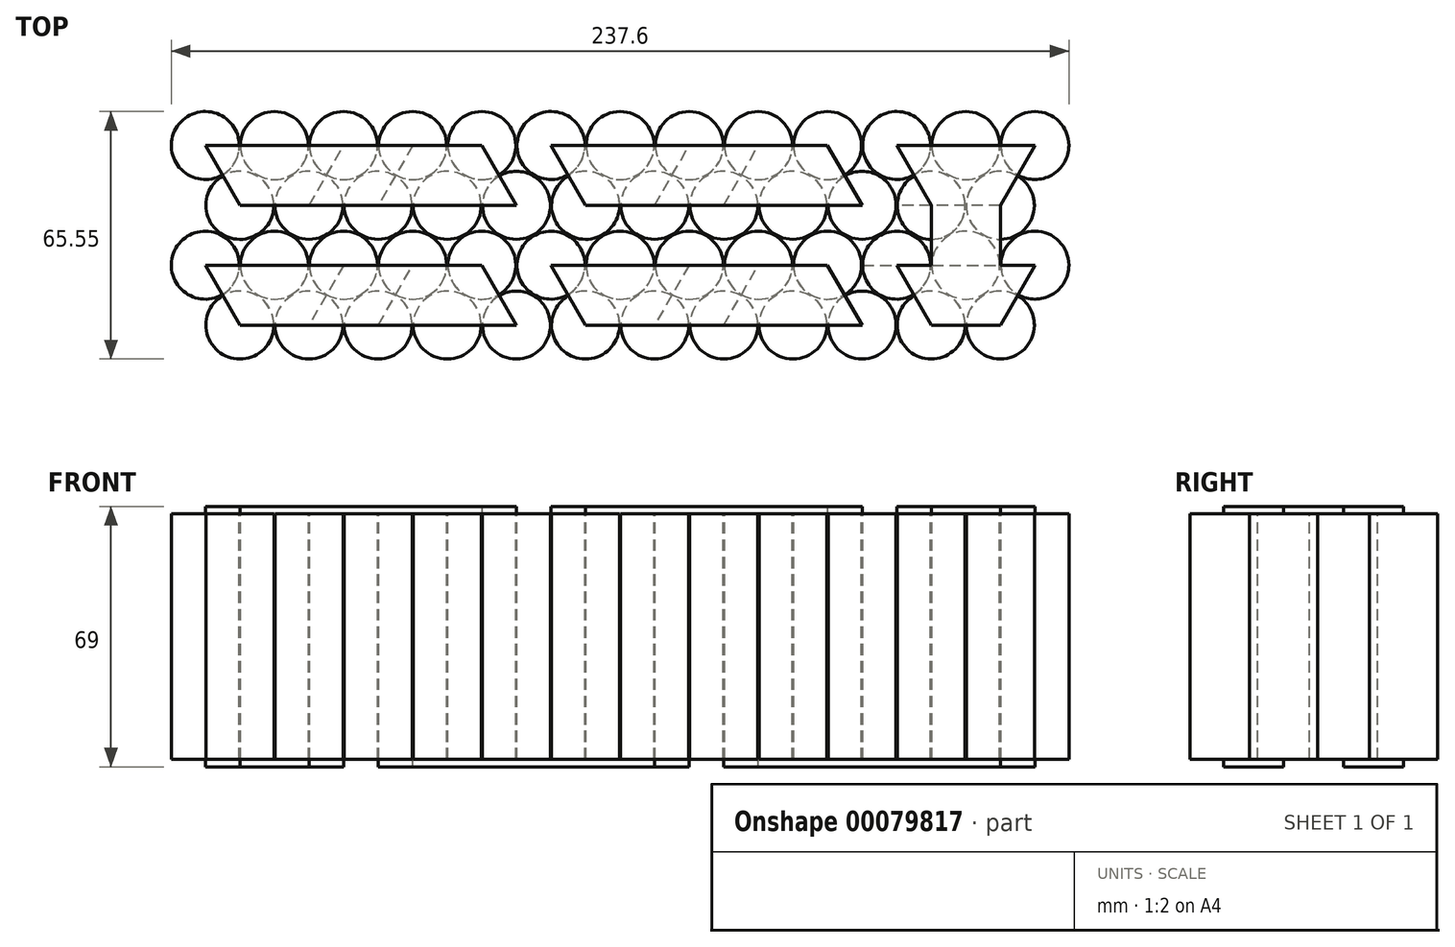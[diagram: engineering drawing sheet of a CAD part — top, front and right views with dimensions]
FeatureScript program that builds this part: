
annotation { "Feature Type Name" : "Feature", "Feature Type Description" : "" }
export const myFeature = defineFeature(function(context is Context, id is Id, definition is map)
    precondition{}
    {
        {
            var Q0;
            Q0=qCreatedBy(makeId("Top.planeOp"),FACE);
            var sketch = newSketch(context, id + "F0", { "sketchPlane" : qUnion([Q0])});
            skLineSegment(sketch, "E0", {"start": v(0, 0) * mm, "end": v(9.15, 15.85) * mm, "construction": true});
            skLineSegment(sketch, "E1", {"start": v(9.15, 15.85) * mm, "end": v(18.3, 0) * mm, "construction": true});
            skLineSegment(sketch, "E2", {"start": v(18.3, 0) * mm, "end": v(9.15, -15.85) * mm, "construction": true});
            skLineSegment(sketch, "E3", {"start": v(9.15, -15.85) * mm, "end": v(0, 0) * mm, "construction": true});
            skLineSegment(sketch, "E4", {"start": v(9.15, 15.85) * mm, "end": v(0, 31.7) * mm, "construction": true});
            skLineSegment(sketch, "E5", {"start": v(0, 31.7) * mm, "end": v(18.3, 31.7) * mm, "construction": true});
            skLineSegment(sketch, "E6", {"start": v(18.3, 31.7) * mm, "end": v(9.15, 15.85) * mm, "construction": true});
            skLineSegment(sketch, "E7", {"start": v(18.3, 31.7) * mm, "end": v(27.45, 15.85) * mm, "construction": true});
            skLineSegment(sketch, "E8", {"start": v(27.45, 15.85) * mm, "end": v(18.3, 0) * mm, "construction": true});
            skLineSegment(sketch, "E9", {"start": v(18.3, 0) * mm, "end": v(27.45, -15.85) * mm, "construction": true});
            skLineSegment(sketch, "E10", {"start": v(27.45, -15.85) * mm, "end": v(9.15, -15.85) * mm, "construction": true});
            skCircle(sketch, "E11", {"center": v(0, 31.7) * mm, "radius": 9 * mm});
            skCircle(sketch, "E12", {"center": v(18.3, 31.7) * mm, "radius": 9 * mm});
            skCircle(sketch, "E13", {"center": v(27.45, 15.85) * mm, "radius": 9 * mm});
            skCircle(sketch, "E14", {"center": v(9.15, 15.85) * mm, "radius": 9 * mm});
            skCircle(sketch, "E15", {"center": v(0, 0) * mm, "radius": 9 * mm});
            skCircle(sketch, "E16", {"center": v(18.3, 0) * mm, "radius": 9 * mm});
            skCircle(sketch, "E17", {"center": v(9.15, -15.85) * mm, "radius": 9 * mm});
            skCircle(sketch, "E18", {"center": v(27.45, -15.85) * mm, "radius": 9 * mm});
            skLineSegment(sketch, "E19", {"start": v(0, 40.7) * mm, "end": v(18.3, 40.7) * mm, "construction": true});
            skLineSegment(sketch, "E20", {"start": v(9.15, -24.85) * mm, "end": v(27.45, -24.85) * mm, "construction": true});
            skCircle(sketch, "E21.1.0.0", {"center": v(54.9, 0) * mm, "radius": 9 * mm});
            skCircle(sketch, "E21.1.0.1", {"center": v(64.05, -15.85) * mm, "radius": 9 * mm});
            skLineSegment(sketch, "E21.1.0.2", {"start": v(45.75, -24.85) * mm, "end": v(64.05, -24.85) * mm, "construction": true});
            skCircle(sketch, "E21.1.0.3", {"center": v(54.9, 31.7) * mm, "radius": 9 * mm});
            skLineSegment(sketch, "E21.1.0.4", {"start": v(54.9, 31.7) * mm, "end": v(64.05, 15.85) * mm, "construction": true});
            skLineSegment(sketch, "E21.1.0.5", {"start": v(64.05, 15.85) * mm, "end": v(54.9, 0) * mm, "construction": true});
            skLineSegment(sketch, "E21.1.0.6", {"start": v(54.9, 31.7) * mm, "end": v(45.75, 15.85) * mm, "construction": true});
            skLineSegment(sketch, "E21.1.0.7", {"start": v(54.9, 0) * mm, "end": v(64.05, -15.85) * mm, "construction": true});
            skLineSegment(sketch, "E21.1.0.8", {"start": v(36.6, 31.7) * mm, "end": v(54.9, 31.7) * mm, "construction": true});
            skLineSegment(sketch, "E21.1.0.9", {"start": v(64.05, -15.85) * mm, "end": v(45.75, -15.85) * mm, "construction": true});
            skLineSegment(sketch, "E21.1.0.10", {"start": v(45.75, 15.85) * mm, "end": v(36.6, 31.7) * mm, "construction": true});
            skLineSegment(sketch, "E21.1.0.11", {"start": v(45.75, -15.85) * mm, "end": v(36.6, 0) * mm, "construction": true});
            skCircle(sketch, "E21.1.0.12", {"center": v(36.6, 31.7) * mm, "radius": 9 * mm});
            skCircle(sketch, "E21.1.0.13", {"center": v(45.75, 15.85) * mm, "radius": 9 * mm});
            skCircle(sketch, "E21.1.0.14", {"center": v(36.6, 0) * mm, "radius": 9 * mm});
            skCircle(sketch, "E21.1.0.15", {"center": v(45.75, -15.85) * mm, "radius": 9 * mm});
            skLineSegment(sketch, "E21.1.0.16", {"start": v(54.9, 0) * mm, "end": v(45.75, -15.85) * mm, "construction": true});
            skLineSegment(sketch, "E21.1.0.17", {"start": v(45.75, 15.85) * mm, "end": v(54.9, 0) * mm, "construction": true});
            skLineSegment(sketch, "E21.1.0.18", {"start": v(36.6, 0) * mm, "end": v(45.75, 15.85) * mm, "construction": true});
            skCircle(sketch, "E21.1.0.19", {"center": v(64.05, 15.85) * mm, "radius": 9 * mm});
            skLineSegment(sketch, "E21.1.0.20", {"start": v(36.6, 40.7) * mm, "end": v(54.9, 40.7) * mm, "construction": true});
            skCircle(sketch, "E21.2.0.0", {"center": v(91.5, 0) * mm, "radius": 9 * mm});
            skCircle(sketch, "E21.2.0.1", {"center": v(100.65, -15.85) * mm, "radius": 9 * mm});
            skLineSegment(sketch, "E21.2.0.2", {"start": v(82.35, -24.85) * mm, "end": v(100.65, -24.85) * mm, "construction": true});
            skCircle(sketch, "E21.2.0.3", {"center": v(91.5, 31.7) * mm, "radius": 9 * mm});
            skLineSegment(sketch, "E21.2.0.4", {"start": v(91.5, 31.7) * mm, "end": v(100.65, 15.85) * mm, "construction": true});
            skLineSegment(sketch, "E21.2.0.5", {"start": v(100.65, 15.85) * mm, "end": v(91.5, 0) * mm, "construction": true});
            skLineSegment(sketch, "E21.2.0.6", {"start": v(91.5, 31.7) * mm, "end": v(82.35, 15.85) * mm, "construction": true});
            skLineSegment(sketch, "E21.2.0.7", {"start": v(91.5, 0) * mm, "end": v(100.65, -15.85) * mm, "construction": true});
            skLineSegment(sketch, "E21.2.0.8", {"start": v(73.2, 31.7) * mm, "end": v(91.5, 31.7) * mm, "construction": true});
            skLineSegment(sketch, "E21.2.0.9", {"start": v(100.65, -15.85) * mm, "end": v(82.35, -15.85) * mm, "construction": true});
            skLineSegment(sketch, "E21.2.0.10", {"start": v(82.35, 15.85) * mm, "end": v(73.2, 31.7) * mm, "construction": true});
            skLineSegment(sketch, "E21.2.0.11", {"start": v(82.35, -15.85) * mm, "end": v(73.2, 0) * mm, "construction": true});
            skCircle(sketch, "E21.2.0.12", {"center": v(73.2, 31.7) * mm, "radius": 9 * mm});
            skCircle(sketch, "E21.2.0.13", {"center": v(82.35, 15.85) * mm, "radius": 9 * mm});
            skCircle(sketch, "E21.2.0.14", {"center": v(73.2, 0) * mm, "radius": 9 * mm});
            skCircle(sketch, "E21.2.0.15", {"center": v(82.35, -15.85) * mm, "radius": 9 * mm});
            skLineSegment(sketch, "E21.2.0.16", {"start": v(91.5, 0) * mm, "end": v(82.35, -15.85) * mm, "construction": true});
            skLineSegment(sketch, "E21.2.0.17", {"start": v(82.35, 15.85) * mm, "end": v(91.5, 0) * mm, "construction": true});
            skLineSegment(sketch, "E21.2.0.18", {"start": v(73.2, 0) * mm, "end": v(82.35, 15.85) * mm, "construction": true});
            skCircle(sketch, "E21.2.0.19", {"center": v(100.65, 15.85) * mm, "radius": 9 * mm});
            skLineSegment(sketch, "E21.2.0.20", {"start": v(73.2, 40.7) * mm, "end": v(91.5, 40.7) * mm, "construction": true});
            skCircle(sketch, "E21.3.0.0", {"center": v(128.1, 0) * mm, "radius": 9 * mm});
            skCircle(sketch, "E21.3.0.1", {"center": v(137.25, -15.85) * mm, "radius": 9 * mm});
            skLineSegment(sketch, "E21.3.0.2", {"start": v(118.95, -24.85) * mm, "end": v(137.25, -24.85) * mm, "construction": true});
            skCircle(sketch, "E21.3.0.3", {"center": v(128.1, 31.7) * mm, "radius": 9 * mm});
            skLineSegment(sketch, "E21.3.0.4", {"start": v(128.1, 31.7) * mm, "end": v(137.25, 15.85) * mm, "construction": true});
            skLineSegment(sketch, "E21.3.0.5", {"start": v(137.25, 15.85) * mm, "end": v(128.1, 0) * mm, "construction": true});
            skLineSegment(sketch, "E21.3.0.6", {"start": v(128.1, 31.7) * mm, "end": v(118.95, 15.85) * mm, "construction": true});
            skLineSegment(sketch, "E21.3.0.7", {"start": v(128.1, 0) * mm, "end": v(137.25, -15.85) * mm, "construction": true});
            skLineSegment(sketch, "E21.3.0.8", {"start": v(109.8, 31.7) * mm, "end": v(128.1, 31.7) * mm, "construction": true});
            skLineSegment(sketch, "E21.3.0.9", {"start": v(137.25, -15.85) * mm, "end": v(118.95, -15.85) * mm, "construction": true});
            skLineSegment(sketch, "E21.3.0.10", {"start": v(118.95, 15.85) * mm, "end": v(109.8, 31.7) * mm, "construction": true});
            skLineSegment(sketch, "E21.3.0.11", {"start": v(118.95, -15.85) * mm, "end": v(109.8, 0) * mm, "construction": true});
            skCircle(sketch, "E21.3.0.12", {"center": v(109.8, 31.7) * mm, "radius": 9 * mm});
            skCircle(sketch, "E21.3.0.13", {"center": v(118.95, 15.85) * mm, "radius": 9 * mm});
            skCircle(sketch, "E21.3.0.14", {"center": v(109.8, 0) * mm, "radius": 9 * mm});
            skCircle(sketch, "E21.3.0.15", {"center": v(118.95, -15.85) * mm, "radius": 9 * mm});
            skLineSegment(sketch, "E21.3.0.16", {"start": v(128.1, 0) * mm, "end": v(118.95, -15.85) * mm, "construction": true});
            skLineSegment(sketch, "E21.3.0.17", {"start": v(118.95, 15.85) * mm, "end": v(128.1, 0) * mm, "construction": true});
            skLineSegment(sketch, "E21.3.0.18", {"start": v(109.8, 0) * mm, "end": v(118.95, 15.85) * mm, "construction": true});
            skCircle(sketch, "E21.3.0.19", {"center": v(137.25, 15.85) * mm, "radius": 9 * mm});
            skLineSegment(sketch, "E21.3.0.20", {"start": v(109.8, 40.7) * mm, "end": v(128.1, 40.7) * mm, "construction": true});
            skCircle(sketch, "E21.4.0.0", {"center": v(164.7, 0) * mm, "radius": 9 * mm});
            skCircle(sketch, "E21.4.0.1", {"center": v(173.85, -15.85) * mm, "radius": 9 * mm});
            skLineSegment(sketch, "E21.4.0.2", {"start": v(155.55, -24.85) * mm, "end": v(173.85, -24.85) * mm, "construction": true});
            skCircle(sketch, "E21.4.0.3", {"center": v(164.7, 31.7) * mm, "radius": 9 * mm});
            skLineSegment(sketch, "E21.4.0.4", {"start": v(164.7, 31.7) * mm, "end": v(173.85, 15.85) * mm, "construction": true});
            skLineSegment(sketch, "E21.4.0.5", {"start": v(173.85, 15.85) * mm, "end": v(164.7, 0) * mm, "construction": true});
            skLineSegment(sketch, "E21.4.0.6", {"start": v(164.7, 31.7) * mm, "end": v(155.55, 15.85) * mm, "construction": true});
            skLineSegment(sketch, "E21.4.0.7", {"start": v(164.7, 0) * mm, "end": v(173.85, -15.85) * mm, "construction": true});
            skLineSegment(sketch, "E21.4.0.8", {"start": v(146.4, 31.7) * mm, "end": v(164.7, 31.7) * mm, "construction": true});
            skLineSegment(sketch, "E21.4.0.9", {"start": v(173.85, -15.85) * mm, "end": v(155.55, -15.85) * mm, "construction": true});
            skLineSegment(sketch, "E21.4.0.10", {"start": v(155.55, 15.85) * mm, "end": v(146.4, 31.7) * mm, "construction": true});
            skLineSegment(sketch, "E21.4.0.11", {"start": v(155.55, -15.85) * mm, "end": v(146.4, 0) * mm, "construction": true});
            skCircle(sketch, "E21.4.0.12", {"center": v(146.4, 31.7) * mm, "radius": 9 * mm});
            skCircle(sketch, "E21.4.0.13", {"center": v(155.55, 15.85) * mm, "radius": 9 * mm});
            skCircle(sketch, "E21.4.0.14", {"center": v(146.4, 0) * mm, "radius": 9 * mm});
            skCircle(sketch, "E21.4.0.15", {"center": v(155.55, -15.85) * mm, "radius": 9 * mm});
            skLineSegment(sketch, "E21.4.0.16", {"start": v(164.7, 0) * mm, "end": v(155.55, -15.85) * mm, "construction": true});
            skLineSegment(sketch, "E21.4.0.17", {"start": v(155.55, 15.85) * mm, "end": v(164.7, 0) * mm, "construction": true});
            skLineSegment(sketch, "E21.4.0.18", {"start": v(146.4, 0) * mm, "end": v(155.55, 15.85) * mm, "construction": true});
            skCircle(sketch, "E21.4.0.19", {"center": v(173.85, 15.85) * mm, "radius": 9 * mm});
            skLineSegment(sketch, "E21.4.0.20", {"start": v(146.4, 40.7) * mm, "end": v(164.7, 40.7) * mm, "construction": true});
            skCircle(sketch, "E21.5.0.0", {"center": v(201.3, 0) * mm, "radius": 9 * mm});
            skCircle(sketch, "E21.5.0.1", {"center": v(210.45, -15.85) * mm, "radius": 9 * mm});
            skLineSegment(sketch, "E21.5.0.2", {"start": v(192.15, -24.85) * mm, "end": v(210.45, -24.85) * mm, "construction": true});
            skCircle(sketch, "E21.5.0.3", {"center": v(201.3, 31.7) * mm, "radius": 9 * mm});
            skLineSegment(sketch, "E21.5.0.4", {"start": v(201.3, 31.7) * mm, "end": v(210.45, 15.85) * mm, "construction": true});
            skLineSegment(sketch, "E21.5.0.5", {"start": v(210.45, 15.85) * mm, "end": v(201.3, 0) * mm, "construction": true});
            skLineSegment(sketch, "E21.5.0.6", {"start": v(201.3, 31.7) * mm, "end": v(192.15, 15.85) * mm, "construction": true});
            skLineSegment(sketch, "E21.5.0.7", {"start": v(201.3, 0) * mm, "end": v(210.45, -15.85) * mm, "construction": true});
            skLineSegment(sketch, "E21.5.0.8", {"start": v(183, 31.7) * mm, "end": v(201.3, 31.7) * mm, "construction": true});
            skLineSegment(sketch, "E21.5.0.9", {"start": v(210.45, -15.85) * mm, "end": v(192.15, -15.85) * mm, "construction": true});
            skLineSegment(sketch, "E21.5.0.10", {"start": v(192.15, 15.85) * mm, "end": v(183, 31.7) * mm, "construction": true});
            skLineSegment(sketch, "E21.5.0.11", {"start": v(192.15, -15.85) * mm, "end": v(183, 0) * mm, "construction": true});
            skCircle(sketch, "E21.5.0.12", {"center": v(183, 31.7) * mm, "radius": 9 * mm});
            skCircle(sketch, "E21.5.0.13", {"center": v(192.15, 15.85) * mm, "radius": 9 * mm});
            skCircle(sketch, "E21.5.0.14", {"center": v(183, 0) * mm, "radius": 9 * mm});
            skCircle(sketch, "E21.5.0.15", {"center": v(192.15, -15.85) * mm, "radius": 9 * mm});
            skLineSegment(sketch, "E21.5.0.16", {"start": v(201.3, 0) * mm, "end": v(192.15, -15.85) * mm, "construction": true});
            skLineSegment(sketch, "E21.5.0.17", {"start": v(192.15, 15.85) * mm, "end": v(201.3, 0) * mm, "construction": true});
            skLineSegment(sketch, "E21.5.0.18", {"start": v(183, 0) * mm, "end": v(192.15, 15.85) * mm, "construction": true});
            skCircle(sketch, "E21.5.0.19", {"center": v(210.45, 15.85) * mm, "radius": 9 * mm});
            skLineSegment(sketch, "E21.5.0.20", {"start": v(183, 40.7) * mm, "end": v(201.3, 40.7) * mm, "construction": true});
            skCircle(sketch, "E21.6.0.12", {"center": v(219.6, 31.7) * mm, "radius": 9 * mm});
            skCircle(sketch, "E21.6.0.14", {"center": v(219.6, 0) * mm, "radius": 9 * mm});
            skLineSegment(sketch, "E21.direction1", {"start": v(9.15, -24.85) * mm, "end": v(45.75, -24.85) * mm, "construction": true});
            skSolve(sketch);
        }
        {
            var Q0;
            Q0=qCreatedBy(makeId("Top.planeOp"),FACE);
            var sketch = newSketch(context, id + "F1", { "sketchPlane" : qUnion([Q0])});
            skLineSegment(sketch, "E22", {"start": v(0, 0) * mm, "end": v(36.6, 0) * mm});
            skLineSegment(sketch, "E23", {"start": v(36.6, 0) * mm, "end": v(27.45, -15.85) * mm, "construction": true});
            skLineSegment(sketch, "E24", {"start": v(27.45, -15.85) * mm, "end": v(9.15, -15.85) * mm});
            skLineSegment(sketch, "E25", {"start": v(9.15, -15.85) * mm, "end": v(0, 0) * mm});
            skLineSegment(sketch, "E26", {"start": v(36.6, 31.7) * mm, "end": v(27.45, 15.85) * mm, "construction": true});
            skLineSegment(sketch, "E27", {"start": v(27.45, 15.85) * mm, "end": v(9.15, 15.85) * mm});
            skLineSegment(sketch, "E28", {"start": v(9.15, 15.85) * mm, "end": v(0, 31.7) * mm});
            skLineSegment(sketch, "E29", {"start": v(0, 31.7) * mm, "end": v(36.6, 31.7) * mm});
            skLineSegment(sketch, "E30", {"start": v(45.75, 15.85) * mm, "end": v(54.9, 31.7) * mm, "construction": true});
            skLineSegment(sketch, "E31", {"start": v(54.9, 31.7) * mm, "end": v(73.2, 31.7) * mm});
            skLineSegment(sketch, "E32", {"start": v(73.2, 31.7) * mm, "end": v(82.35, 15.85) * mm});
            skLineSegment(sketch, "E33", {"start": v(82.35, 15.85) * mm, "end": v(45.75, 15.85) * mm});
            skLineSegment(sketch, "E34", {"start": v(54.9, 0) * mm, "end": v(73.2, 0) * mm});
            skLineSegment(sketch, "E35", {"start": v(73.2, 0) * mm, "end": v(82.35, -15.85) * mm});
            skLineSegment(sketch, "E36", {"start": v(82.35, -15.85) * mm, "end": v(45.75, -15.85) * mm});
            skLineSegment(sketch, "E37", {"start": v(45.75, -15.85) * mm, "end": v(54.9, 0) * mm, "construction": true});
            skLineSegment(sketch, "E38", {"start": v(183, 0) * mm, "end": v(192.15, 0) * mm});
            skLineSegment(sketch, "E39", {"start": v(219.6, 0) * mm, "end": v(210.45, -15.85) * mm});
            skLineSegment(sketch, "E40", {"start": v(210.45, -15.85) * mm, "end": v(192.15, -15.85) * mm});
            skLineSegment(sketch, "E41", {"start": v(192.15, -15.85) * mm, "end": v(183, 0) * mm});
            skLineSegment(sketch, "E42", {"start": v(192.15, 15.85) * mm, "end": v(210.45, 15.85) * mm, "construction": true});
            skLineSegment(sketch, "E43", {"start": v(210.45, 15.85) * mm, "end": v(219.6, 31.7) * mm});
            skLineSegment(sketch, "E44", {"start": v(219.6, 31.7) * mm, "end": v(183, 31.7) * mm});
            skLineSegment(sketch, "E45", {"start": v(183, 31.7) * mm, "end": v(192.15, 15.85) * mm});
            skLineSegment(sketch, "E46.1.0.0", {"start": v(118.95, -15.85) * mm, "end": v(100.65, -15.85) * mm});
            skLineSegment(sketch, "E46.1.0.1", {"start": v(137.25, -15.85) * mm, "end": v(146.4, 0) * mm, "construction": true});
            skLineSegment(sketch, "E46.1.0.2", {"start": v(100.65, 15.85) * mm, "end": v(91.5, 31.7) * mm});
            skLineSegment(sketch, "E46.1.0.3", {"start": v(128.1, 0) * mm, "end": v(118.95, -15.85) * mm, "construction": true});
            skLineSegment(sketch, "E46.1.0.4", {"start": v(118.95, 15.85) * mm, "end": v(100.65, 15.85) * mm});
            skLineSegment(sketch, "E46.1.0.5", {"start": v(164.7, 0) * mm, "end": v(173.85, -15.85) * mm});
            skLineSegment(sketch, "E46.1.0.6", {"start": v(137.25, 15.85) * mm, "end": v(146.4, 31.7) * mm, "construction": true});
            skLineSegment(sketch, "E46.1.0.7", {"start": v(146.4, 31.7) * mm, "end": v(164.7, 31.7) * mm});
            skLineSegment(sketch, "E46.1.0.8", {"start": v(100.65, -15.85) * mm, "end": v(91.5, 0) * mm});
            skLineSegment(sketch, "E46.1.0.9", {"start": v(128.1, 31.7) * mm, "end": v(118.95, 15.85) * mm, "construction": true});
            skLineSegment(sketch, "E46.1.0.10", {"start": v(173.85, -15.85) * mm, "end": v(137.25, -15.85) * mm});
            skLineSegment(sketch, "E46.1.0.11", {"start": v(91.5, 0) * mm, "end": v(128.1, 0) * mm});
            skLineSegment(sketch, "E46.1.0.12", {"start": v(91.5, 31.7) * mm, "end": v(128.1, 31.7) * mm});
            skLineSegment(sketch, "E46.1.0.13", {"start": v(164.7, 31.7) * mm, "end": v(173.85, 15.85) * mm});
            skLineSegment(sketch, "E46.1.0.14", {"start": v(173.85, 15.85) * mm, "end": v(137.25, 15.85) * mm});
            skLineSegment(sketch, "E46.1.0.15", {"start": v(146.4, 0) * mm, "end": v(164.7, 0) * mm});
            skLineSegment(sketch, "E46.direction1", {"start": v(9.15, -15.85) * mm, "end": v(100.65, -15.85) * mm, "construction": true});
            skLineSegment(sketch, "E47", {"start": v(36.6, 31.7) * mm, "end": v(54.9, 31.7) * mm});
            skLineSegment(sketch, "E48", {"start": v(27.45, 15.85) * mm, "end": v(45.75, 15.85) * mm});
            skLineSegment(sketch, "E49", {"start": v(36.6, 0) * mm, "end": v(54.9, 0) * mm});
            skLineSegment(sketch, "E50", {"start": v(27.45, -15.85) * mm, "end": v(45.75, -15.85) * mm});
            skLineSegment(sketch, "E51", {"start": v(128.1, 0) * mm, "end": v(146.4, 0) * mm});
            skLineSegment(sketch, "E52", {"start": v(118.95, -15.85) * mm, "end": v(137.25, -15.85) * mm});
            skLineSegment(sketch, "E53", {"start": v(128.1, 31.7) * mm, "end": v(146.4, 31.7) * mm});
            skLineSegment(sketch, "E54", {"start": v(118.95, 15.85) * mm, "end": v(137.25, 15.85) * mm});
            skLineSegment(sketch, "E55", {"start": v(192.15, 15.85) * mm, "end": v(192.15, 0) * mm});
            skLineSegment(sketch, "E56", {"start": v(210.45, 15.85) * mm, "end": v(210.45, 0) * mm});
            skLineSegment(sketch, "E57.trimOffspring", {"start": v(210.45, 0) * mm, "end": v(219.6, 0) * mm});
            skSolve(sketch);
        }
        {
            var Q0;
            Q0 = qSketchRegion(id + "F1", true);
            extrude(context, id + "F2", {"entities" : qUnion([Q0]), "depth" : 2 * mm});
        }
        {
            var Q0;
            Q0 = qSketchRegion(id + "F0", true);
            extrude(context, id + "F3", {"entities" : qUnion([Q0]), "oppositeDirection" : true, "depth" : 65 * mm});
        }
        {
            var Q0;
            Q0=makeQuery(id+"F3.opExtrude","CAP_FACE",FACE,{"disambiguationData":[OSD([sQuery(id+"F0.wireOp",EDGE,"E11")])],"isStart":false});
            var sketch = newSketch(context, id + "F4", { "sketchPlane" : qUnion([Q0])});
            skLineSegment(sketch, "E58", {"start": v(0, -31.7) * mm, "end": v(9.15, -15.85) * mm});
            skLineSegment(sketch, "E59", {"start": v(9.15, -15.85) * mm, "end": v(27.45, -15.85) * mm});
            skLineSegment(sketch, "E60", {"start": v(27.45, -15.85) * mm, "end": v(36.6, -31.7) * mm});
            skLineSegment(sketch, "E61", {"start": v(36.6, -31.7) * mm, "end": v(0, -31.7) * mm});
            skLineSegment(sketch, "E62", {"start": v(0, 0) * mm, "end": v(36.6, 0) * mm});
            skLineSegment(sketch, "E63", {"start": v(36.6, 0) * mm, "end": v(27.45, 15.85) * mm});
            skLineSegment(sketch, "E64", {"start": v(27.45, 15.85) * mm, "end": v(9.15, 15.85) * mm});
            skLineSegment(sketch, "E65", {"start": v(9.15, 15.85) * mm, "end": v(0, 0) * mm});
            skLineSegment(sketch, "E66", {"start": v(45.75, 15.85) * mm, "end": v(54.9, 0) * mm});
            skLineSegment(sketch, "E67", {"start": v(54.9, 0) * mm, "end": v(128.1, 0) * mm});
            skLineSegment(sketch, "E68", {"start": v(128.1, 0) * mm, "end": v(118.95, 15.85) * mm});
            skLineSegment(sketch, "E69", {"start": v(118.95, 15.85) * mm, "end": v(45.75, 15.85) * mm});
            skLineSegment(sketch, "E70", {"start": v(45.75, -15.85) * mm, "end": v(118.95, -15.85) * mm});
            skLineSegment(sketch, "E71", {"start": v(118.95, -15.85) * mm, "end": v(128.1, -31.7) * mm});
            skLineSegment(sketch, "E72", {"start": v(128.1, -31.7) * mm, "end": v(54.9, -31.7) * mm});
            skLineSegment(sketch, "E73", {"start": v(54.9, -31.7) * mm, "end": v(45.75, -15.85) * mm});
            skLineSegment(sketch, "E74", {"start": v(137.25, 15.85) * mm, "end": v(146.4, 0) * mm});
            skLineSegment(sketch, "E75", {"start": v(146.4, 0) * mm, "end": v(219.6, 0) * mm});
            skLineSegment(sketch, "E76", {"start": v(219.6, 0) * mm, "end": v(210.45, 15.85) * mm});
            skLineSegment(sketch, "E77", {"start": v(210.45, 15.85) * mm, "end": v(137.25, 15.85) * mm});
            skLineSegment(sketch, "E78", {"start": v(137.25, -15.85) * mm, "end": v(146.4, -31.7) * mm});
            skLineSegment(sketch, "E79", {"start": v(146.4, -31.7) * mm, "end": v(219.6, -31.7) * mm});
            skLineSegment(sketch, "E80", {"start": v(219.6, -31.7) * mm, "end": v(210.45, -15.85) * mm});
            skLineSegment(sketch, "E81", {"start": v(210.45, -15.85) * mm, "end": v(137.25, -15.85) * mm});
            skSolve(sketch);
        }
        {
            var Q0;
            Q0 = qSketchRegion(id + "F4", true);
            extrude(context, id + "F5", {"entities" : qUnion([Q0]), "depth" : 2 * mm});
        }
    });
